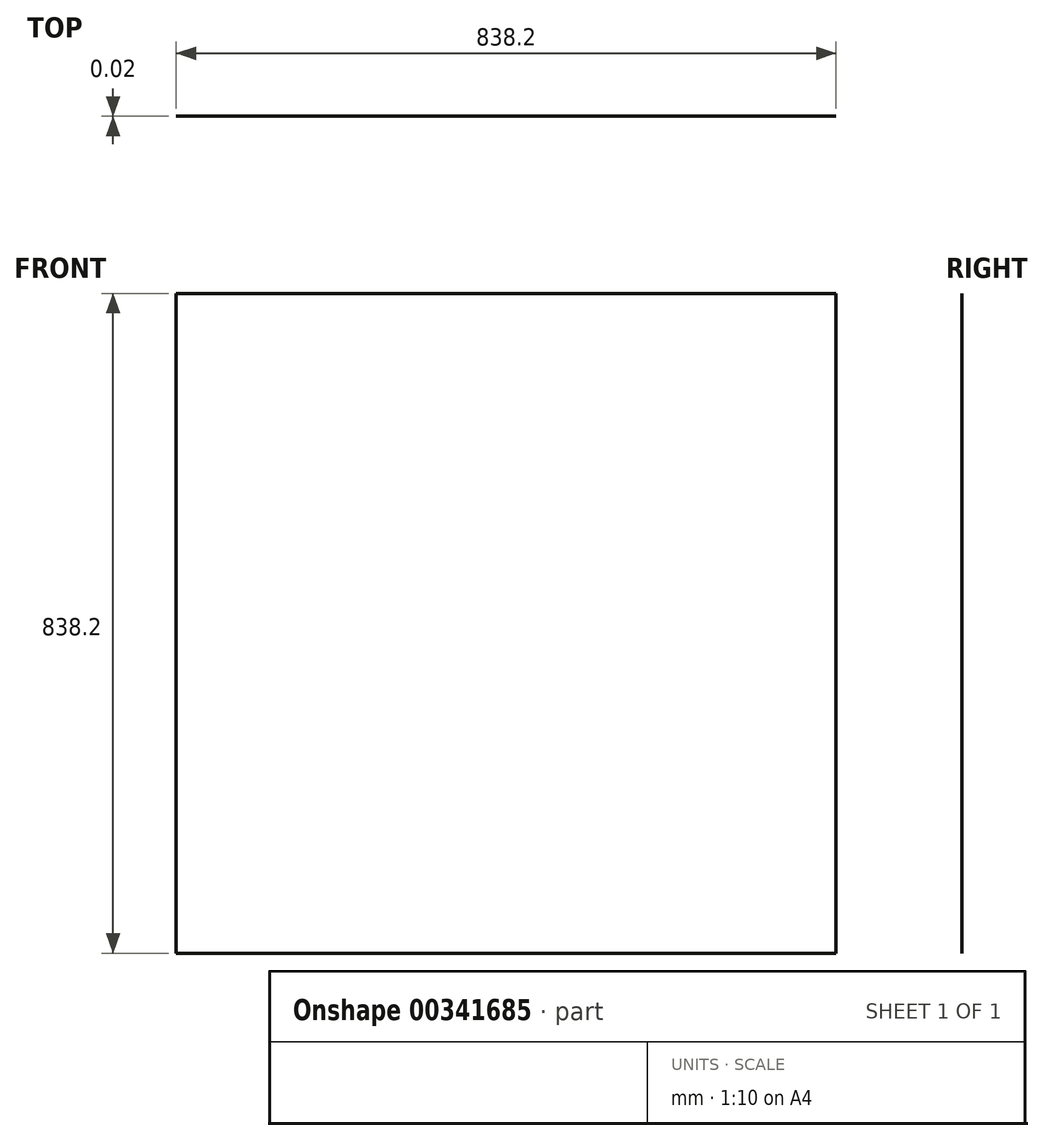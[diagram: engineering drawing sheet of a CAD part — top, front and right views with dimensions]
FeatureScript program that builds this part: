
annotation { "Feature Type Name" : "Feature", "Feature Type Description" : "" }
export const myFeature = defineFeature(function(context is Context, id is Id, definition is map)
    precondition{}
    {
        {
            var Q0;
            Q0=qCreatedBy(makeId("Front.planeOp"),FACE);
            var sketch = newSketch(context, id + "F0", { "sketchPlane" : qUnion([Q0])});
            skLineSegment(sketch, "E0.bottom", {"start": v(414.93, 391.12) * mm, "end": v(-423.27, 391.12) * mm});
            skLineSegment(sketch, "E0.top", {"start": v(414.93, -447.08) * mm, "end": v(-423.27, -447.08) * mm});
            skLineSegment(sketch, "E0.left", {"start": v(414.93, 391.12) * mm, "end": v(414.93, -447.08) * mm});
            skLineSegment(sketch, "E0.right", {"start": v(-423.27, 391.12) * mm, "end": v(-423.27, -447.08) * mm});
            skSolve(sketch);
        }
        {
            var Q0;
            Q0=makeQuery(id+"F0.imprint","IMPRINT",FACE,{"disambiguationData":[TD([[makeQuery(id+"F0.imprint","IMPRINT",EDGE,{"derivedFrom":sQuery(id+"F0.wireOp",EDGE,"E0.bottom")}),1.0]])]});
            extrude(context, id + "F1", {"entities" : qUnion([Q0]), "depth" : 1 / 50.8 * mm});
        }
    });
